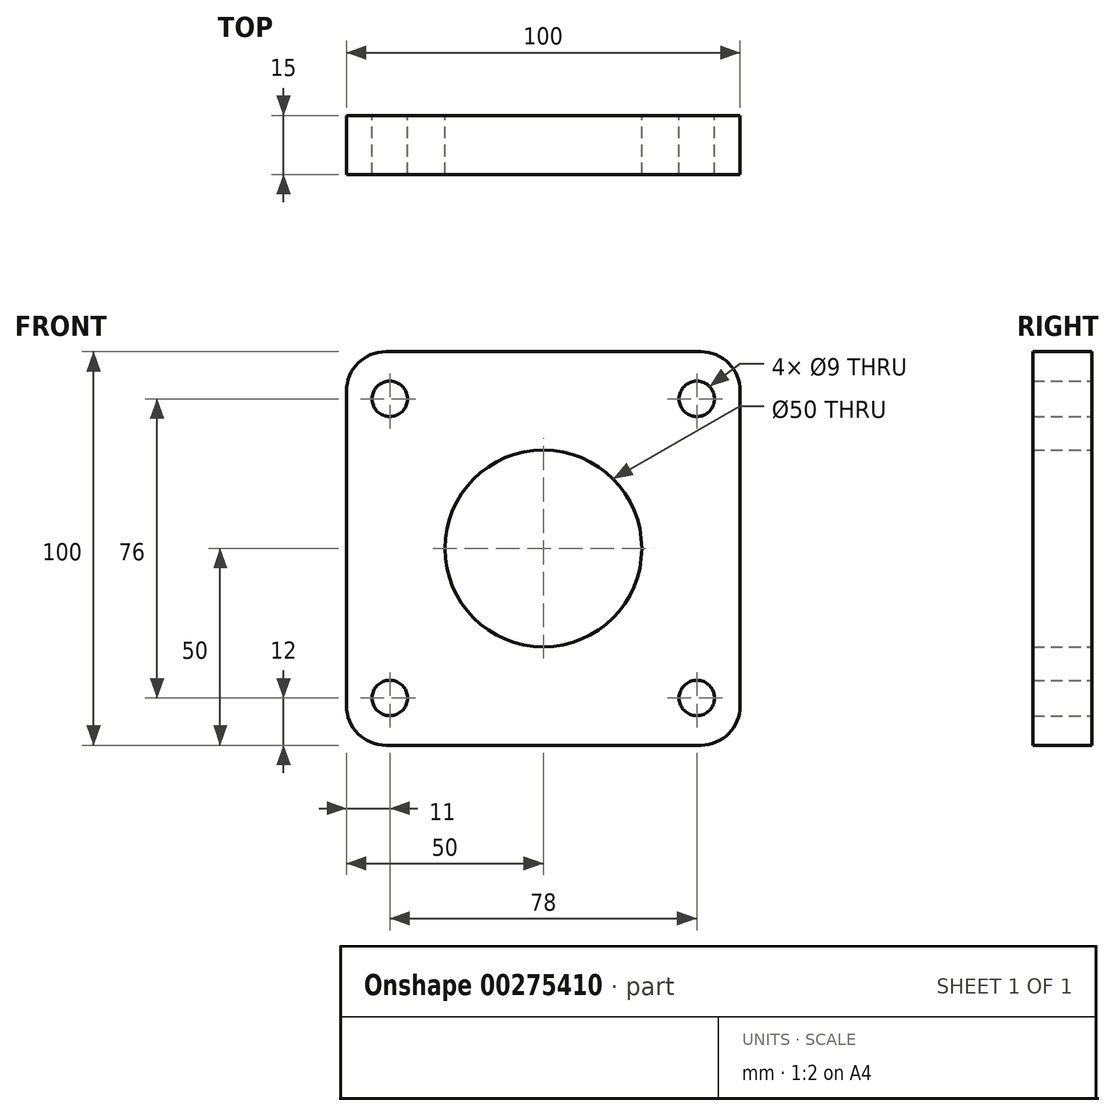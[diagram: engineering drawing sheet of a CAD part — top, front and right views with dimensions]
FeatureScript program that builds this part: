
annotation { "Feature Type Name" : "Feature", "Feature Type Description" : "" }
export const myFeature = defineFeature(function(context is Context, id is Id, definition is map)
    precondition{}
    {
        {
            var Q0;
            Q0=qCreatedBy(makeId("Front.planeOp"),FACE);
            var sketch = newSketch(context, id + "F0", { "sketchPlane" : qUnion([Q0])});
            skLineSegment(sketch, "E0.bottom", {"start": v(-40, 50) * mm, "end": v(40, 50) * mm});
            skLineSegment(sketch, "E0.top", {"start": v(-40, -50) * mm, "end": v(40, -50) * mm});
            skLineSegment(sketch, "E0.left", {"start": v(-50, 40) * mm, "end": v(-50, -40) * mm});
            skLineSegment(sketch, "E0.right", {"start": v(50, 40) * mm, "end": v(50, -40) * mm});
            skPoint(sketch, "E1.visualSharp", {"position": v(-50, 50) * mm});
            skArc(sketch, "E1.filletArc", {"start": v(-40, 50) * mm, "mid": v(-47.07, 47.07) * mm, "end": v(-50, 40) * mm});
            skPoint(sketch, "E2.visualSharp", {"position": v(50, 50) * mm});
            skArc(sketch, "E2.filletArc", {"start": v(50, 40) * mm, "mid": v(47.07, 47.07) * mm, "end": v(40, 50) * mm});
            skPoint(sketch, "E3.visualSharp", {"position": v(50, -50) * mm});
            skArc(sketch, "E3.filletArc", {"start": v(40, -50) * mm, "mid": v(47.07, -47.07) * mm, "end": v(50, -40) * mm});
            skPoint(sketch, "E4.visualSharp", {"position": v(-50, -50) * mm});
            skArc(sketch, "E4.filletArc", {"start": v(-50, -40) * mm, "mid": v(-47.07, -47.07) * mm, "end": v(-40, -50) * mm});
            skCircle(sketch, "E5", {"center": v(0, 0) * mm, "radius": 25 * mm});
            skCircle(sketch, "E6", {"center": v(-39, 38) * mm, "radius": 4.5 * mm});
            skCircle(sketch, "E7", {"center": v(39, 38) * mm, "radius": 4.5 * mm});
            skCircle(sketch, "E8", {"center": v(-39, -38) * mm, "radius": 4.5 * mm});
            skPoint(sketch, "E9.center.orphan", {"position": v(35, -38) * mm});
            skCircle(sketch, "E10", {"center": v(39, -38) * mm, "radius": 4.5 * mm});
            skSolve(sketch);
        }
        {
            var Q0;
            Q0=makeQuery(id+"F0.imprint","IMPRINT",FACE,{"disambiguationData":[TD([[makeQuery(id+"F0.imprint","IMPRINT",EDGE,{"derivedFrom":sQuery(id+"F0.wireOp",EDGE,"E0.bottom")}),-1.0]])]});
            extrude(context, id + "F1", {"entities" : qUnion([Q0]), "depth" : 15 * mm});
        }
    });
